# Revit family: Fitting-U_Shape-Unistrut-P2800-25
name_source: partatom
category: Specialty Equipment
revit_build: Autodesk Revit MEP 2012 (Build: 20110309_2315(x64)
units: mm (PartAtom-declared; Revit-internal decimal feet)

## types (5) — shared parameters
04 CSI = 26 05 48
95 CSI = 16070
Allowable Moment = 0.00 N-m
Assembly Code = D5020100
CAD URL = http://unistrut.us
Category = Specialty Equipment
Literature URL = http://unistrut.us
Load Capacity Note = Visit the product page for load application and capacity.
Manufacturer = Unistrut by Atkore International
Manufacturer Fax = 708-339-7814
Overall Height = 15/32"
Overall Length = 1 5/8"
Overall Width = 2 5/32"
Part Type = Fitting
Power Strut Part Number = PS 623
Product Page URL = http://unistrut.us
Subcategory = U Shape Fittings
Thickness = 1/4"
URL = http://unistrut.us
Unistrut Part Number = P2800-25
Unit = <By Category>
ecoScorecard Product Page = http://products.ecoscorecard.com
ecoScorecard_data = http://products.ecoscorecard.com

## per-type parameters (varying)
| type | Bolt Size | Hole Diameter | Hole Radius | Weight Per Piece |
| P2800-25 | 1/4" | 9/32" | 9/64" | 0.14 lb |
| P2800-37 | 3/8" | 7/16" | 7/32" | 0.14 lb |
| P2800-50 | 1/2" | 9/16" | 9/32" | 0.13 lb |
| P2800-62 | 5/8" | 11/16" | 11/32" | 0.13 lb |
| P2800-75 | 3/4" | 13/16" | 13/32" | 0.13 lb |

note: column(s) folded — value = type name in every type: Model

## geometry (parser evidence)
native form markers: Sweep x4
no freeform markers — native parametric forms only
